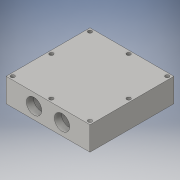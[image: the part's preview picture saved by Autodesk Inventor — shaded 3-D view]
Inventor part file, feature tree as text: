
AUTODESK INVENTOR PART (.ipt)
format: ipt  version: 2016 (Build 200138000, 138)  size: 125,952 bytes
history: native  units: in
note: dims shown in document units (in); Inventor stores cm internally (conversion verified against a paired STEP export)
features: extrude x3, sketch x3
ambient origin geometry x8: Origin, YZ Plane, XZ Plane, XY Plane, X Axis, Y Axis, Z Axis, Center Point
bodies: Solid1 (feature_tree)
feature tree (6):
  extrude  "Extrusion1"  Depth=3.0in
  extrude  "Extrusion2"  Depth=0.85in
  extrude  "Extrusion3"  Depth=0.25in
  sketch  "Sketch1"  dims[d0=3.0in d1=3.0in]
  sketch  "Sketch2"  dims[d2=0.85in d3=0.0in d5=0.119in]
  sketch  "Sketch3"  dims[d6=0.119in d7=0.119in d8=0.119in d9=0.138in d10=0.138in d11=0.138in d12=0.138in d13=0.138in d14=0.138in d15=0.138in d16=0.138in d17=0.45in d18=0.0in d21=0.55in d22=0.55in d23=0.25in d24=0.0in]
